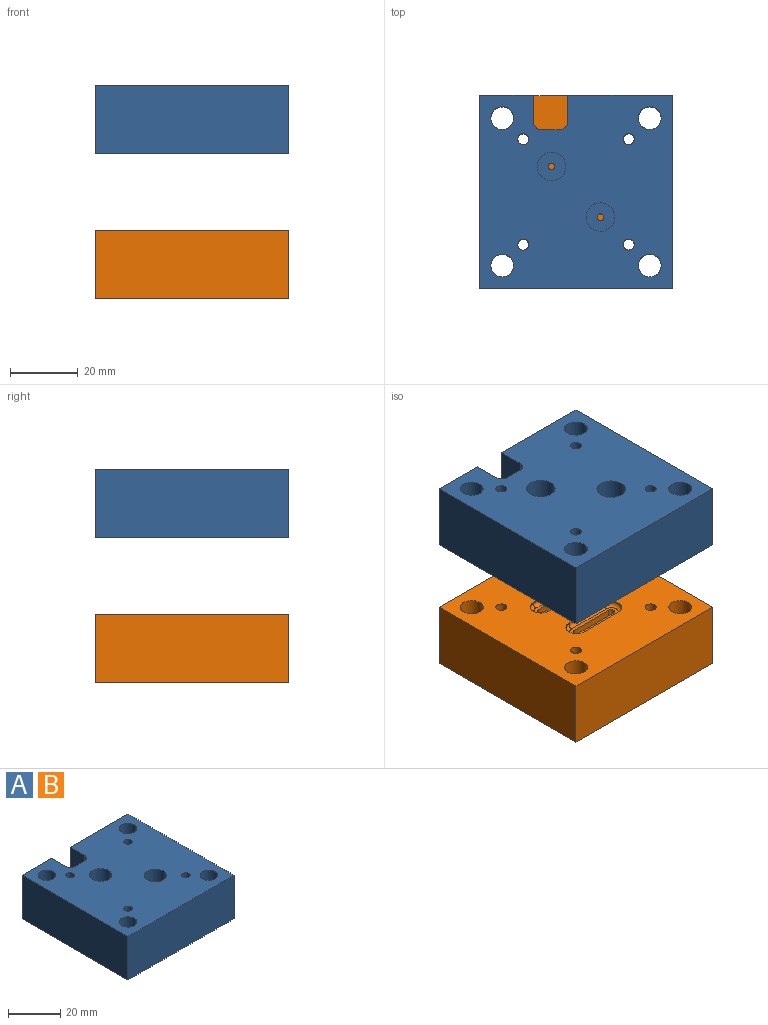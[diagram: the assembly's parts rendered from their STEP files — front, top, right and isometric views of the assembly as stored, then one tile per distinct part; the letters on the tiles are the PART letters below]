
ASSEMBLY  parts=2 mates=1
PART A: 52 faces, bbox 57.2x57.2x20.8 mm
  f0: cylinder r=1mm len=8.64mm, axis (0,0,-1), area 36.6mm2, adj f2,f30,f32,f33,f49
  f1: cylinder r=1mm len=8.64mm, axis (0,0,-1), area 36.6mm2, adj f25,f34,f35,f37,f47
  f2: plane 18.57x4.06mm, normal (0,0,-1), area 39.8mm2, adj f0,f30,f31,f32,f42,f43,f44,f45
  f3: plane 20.32x15.93mm, normal (0,1,0), area 323.7mm2, adj f4,f18,f19,f20
  f4: plane 57.15x20.32mm, normal (-1,0,0), area 1161.3mm2, adj f3,f5,f19,f20
  f5: plane 57.15x20.32mm, normal (0,-1,0), area 1161.3mm2, adj f4,f6,f19,f20
  f6: plane 57.15x20.32mm, normal (1,0,0), area 1161.3mm2, adj f5,f7,f19,f20
  f7: plane 31.06x20.32mm, normal (0,1,0), area 631.1mm2, adj f6,f8,f19,f20
  f8: plane 20.32x7.62mm, normal (-1,0,0), area 154.8mm2, adj f7,f19,f20,f50
  f9: plane 20.32x5.08mm, normal (0,1,0), area 103.2mm2, adj f19,f20,f50,f51
  f10: cylinder r=1.63mm len=20.32mm, axis (0,0,-1), area 208.4mm2, adj f19,f20
  f11: cylinder r=1.63mm len=20.32mm, axis (0,0,-1), area 208.4mm2, adj f19,f20
  f12: cylinder r=1.63mm len=20.32mm, axis (0,0,-1), area 208.4mm2, adj f19,f20
  f13: cylinder r=1.63mm len=20.32mm, axis (0,0,-1), area 208.4mm2, adj f19,f20
  f14: cylinder r=3.38mm len=20.32mm, axis (0,0,-1), area 431.3mm2, adj f19,f20
  f15: cylinder r=3.38mm len=20.32mm, axis (0,0,-1), area 431.3mm2, adj f19,f20
  f16: cylinder r=3.38mm len=20.32mm, axis (0,0,-1), area 431.3mm2, adj f19,f20
  f17: cylinder r=3.38mm len=20.32mm, axis (0,0,-1), area 431.3mm2, adj f19,f20
  f18: plane 20.32x7.62mm, normal (1,0,0), area 154.8mm2, adj f3,f19,f20,f51
  f19: plane 57.15x57.15mm, normal (0,0,1), area 2877.1mm2, adj f3,f4,f5,f6,f7,f8,f9,f10
  f20: plane 57.15x57.15mm, normal (0,0,-1), area 2741.2mm2, adj f3,f4,f5,f6,f7,f8,f9,f10
  f21: plane 14.51x0.38mm, normal (0,-1,0), area 5.5mm2, adj f20,f22,f24,f40
  f22: cylinder r=3.17mm len=6.35mm, axis (0,0,-1), area 3.8mm2, adj f20,f21,f23,f41
  f23: plane 14.51x0.38mm, normal (0,1,0), area 5.5mm2, adj f20,f22,f24,f39
  f24: cylinder r=3.17mm len=6.35mm, axis (0,0,-1), area 3.8mm2, adj f20,f21,f23,f38
  f25: plane 18.57x4.06mm, normal (0,0,-1), area 39.8mm2, adj f1,f34,f35,f36,f38,f39,f40,f41
  f26: plane 14.51x0.38mm, normal (0,1,0), area 5.5mm2, adj f20,f27,f29,f43
  f27: cylinder r=3.17mm len=6.35mm, axis (0,0,-1), area 3.8mm2, adj f20,f26,f28,f42
  f28: plane 14.51x0.38mm, normal (0,-1,0), area 5.5mm2, adj f20,f27,f29,f44
  f29: cylinder r=3.17mm len=6.35mm, axis (0,0,-1), area 3.8mm2, adj f20,f26,f28,f45
  f30: plane 14.51x5.62mm, normal (0,-1,0), area 81.5mm2, adj f0,f2,f31,f33
  f31: cylinder r=1mm len=5.62mm, axis (0,0,-1), area 17.7mm2, adj f2,f30,f32,f33
  f32: plane 14.51x5.62mm, normal (0,1,0), area 81.5mm2, adj f0,f2,f31,f33
  f33: plane 15.51x2mm, normal (0,0,-1), area 29mm2, adj f0,f30,f31,f32
  f34: plane 14.51x5.62mm, normal (0,-1,0), area 81.5mm2, adj f1,f25,f36,f37
  f35: plane 14.51x5.62mm, normal (0,1,0), area 81.5mm2, adj f1,f25,f36,f37
  f36: cylinder r=1mm len=5.62mm, axis (0,0,-1), area 17.7mm2, adj f25,f34,f35,f37
  f37: plane 15.51x2mm, normal (0,0,-1), area 29mm2, adj f1,f34,f35,f36
  f38: torus R=2.03mm, axis (0,0,-1), area 15.6mm2, adj f24,f25,f39,f40
  f39: cylinder r=1.14mm len=14.51mm, axis (-1,0,0), area 26.1mm2, adj f23,f25,f38,f41
  f40: cylinder r=1.14mm len=14.51mm, axis (1,0,0), area 26.1mm2, adj f21,f25,f38,f41
  f41: torus R=2.03mm, axis (0,0,-1), area 15.6mm2, adj f22,f25,f39,f40
  f42: torus R=2.03mm, axis (0,0,-1), area 15.6mm2, adj f2,f27,f43,f44
  f43: cylinder r=1.14mm len=14.51mm, axis (-1,0,0), area 26.1mm2, adj f2,f26,f42,f45
  f44: cylinder r=1.14mm len=14.51mm, axis (1,0,0), area 26.1mm2, adj f2,f28,f42,f45
  f45: torus R=2.03mm, axis (0,0,-1), area 15.6mm2, adj f2,f29,f43,f44
  f46: cylinder r=4.22mm len=10.16mm, axis (0,0,1), area 269.2mm2, adj f19,f47
  f47: plane 8.43x8.43mm, normal (0,0,1), area 52.7mm2, adj f1,f46
  f48: cylinder r=4.22mm len=10.16mm, axis (0,0,1), area 269.2mm2, adj f19,f49
  f49: plane 8.43x8.43mm, normal (0,0,1), area 52.7mm2, adj f0,f48
  f50: cylinder r=2.54mm len=20.32mm, axis (0,0,1), area 81.1mm2, adj f8,f9,f19,f20
  f51: cylinder r=2.54mm len=20.32mm, axis (0,0,-1), area 81.1mm2, adj f9,f18,f19,f20
PART B: same geometry as A
PLACE A t=(-41.55,-35.6,1.35)mm
PLACE B rot(axis=(0,1,0),180deg) t=(15.6,-35.6,-21.24)mm
MATE cylindrical B.f16 <-> A.f15  axis (0,0,-1) through (8.86,14.81,-41.56)mm
